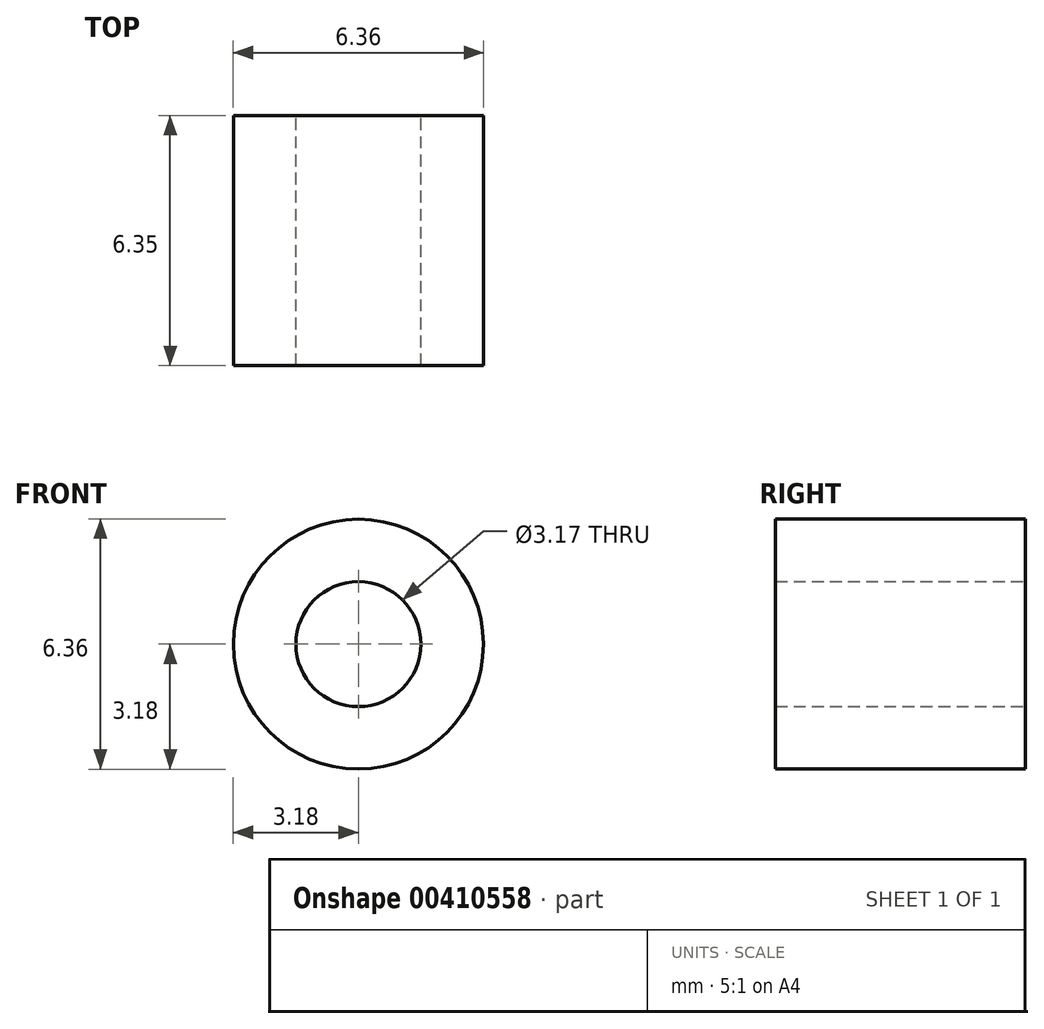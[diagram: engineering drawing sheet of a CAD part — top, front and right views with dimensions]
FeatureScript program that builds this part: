
annotation { "Feature Type Name" : "Feature", "Feature Type Description" : "" }
export const myFeature = defineFeature(function(context is Context, id is Id, definition is map)
    precondition{}
    {
        {
            var Q0;
            Q0=qCreatedBy(makeId("Front.planeOp"),FACE);
            var sketch = newSketch(context, id + "F0", { "sketchPlane" : qUnion([Q0])});
            skCircle(sketch, "E0", {"center": v(0, 0) * mm, "radius": 1.59 * mm});
            skCircle(sketch, "E1", {"center": v(0, 0) * mm, "radius": 3.18 * mm});
            skSolve(sketch);
        }
        {
            var Q0;
            Q0=qSketchRegion(id+"F0",true);
            extrude(context, id + "F1", {"entities" : qUnion([Q0]), "depth" : 6.35 * mm});
        }
    });
